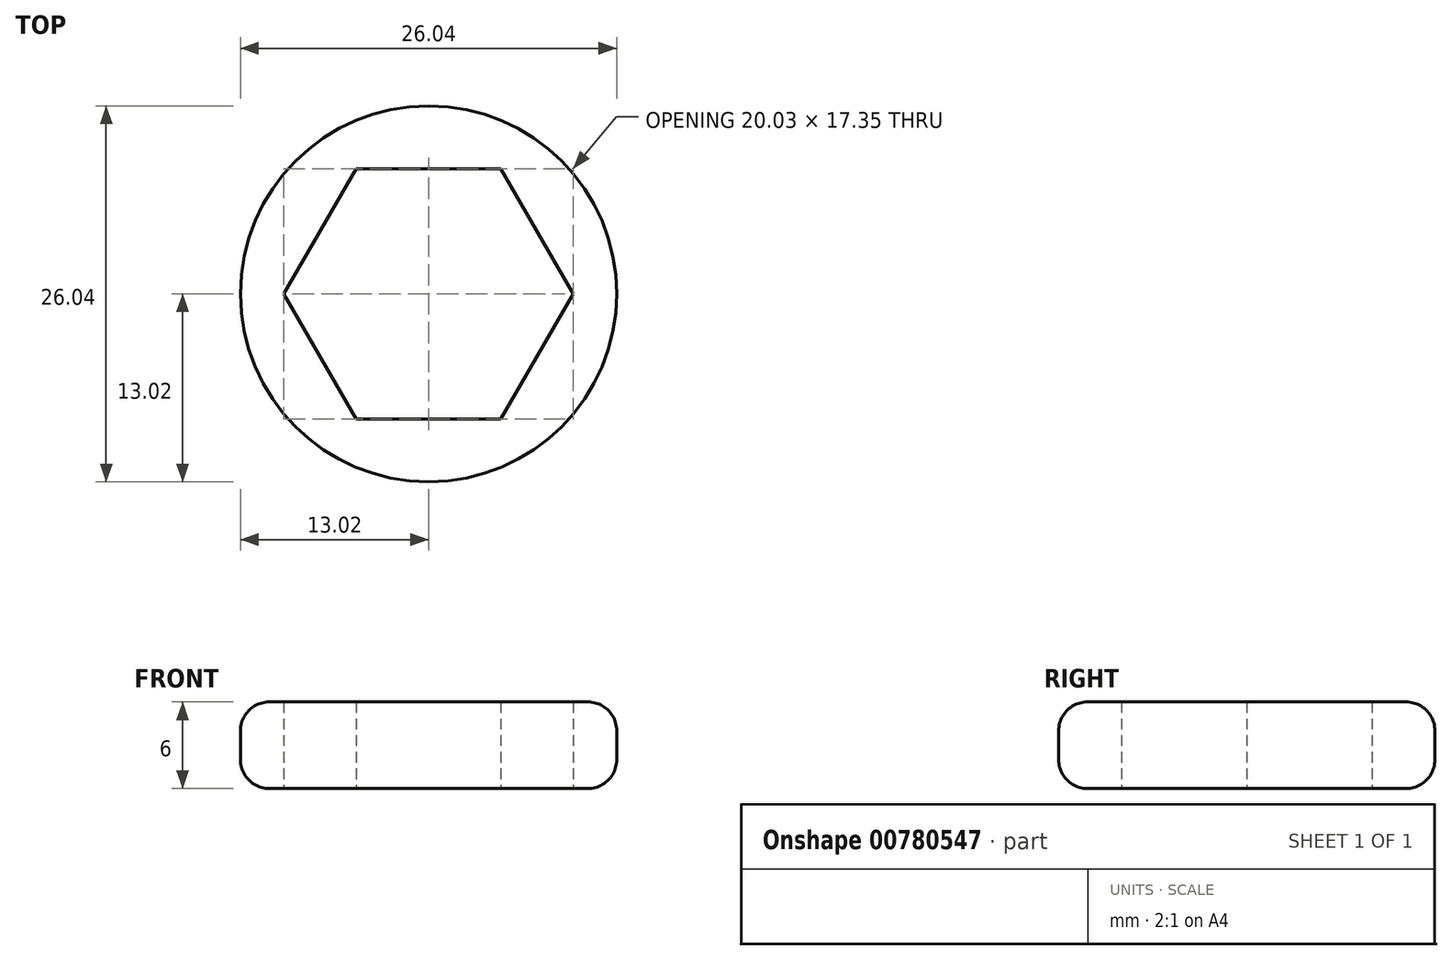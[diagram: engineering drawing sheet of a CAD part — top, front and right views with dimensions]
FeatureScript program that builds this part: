
annotation { "Feature Type Name" : "Feature", "Feature Type Description" : "" }
export const myFeature = defineFeature(function(context is Context, id is Id, definition is map)
    precondition{}
    {
        {
            var Q0;
            Q0=qCreatedBy(makeId("Top.planeOp"),FACE);
            var sketch = newSketch(context, id + "F0", { "sketchPlane" : qUnion([Q0])});
            skCircle(sketch, "E0.cCircle", {"center": v(0, 0) * mm, "radius": 8.68 * mm, "construction": true});
            skLineSegment(sketch, "E0.0", {"start": v(-5, 8.68) * mm, "end": v(5, 8.68) * mm});
            skLineSegment(sketch, "E0.1", {"start": v(5, 8.68) * mm, "end": v(10.02, 0) * mm});
            skLineSegment(sketch, "E0.2", {"start": v(10.02, 0) * mm, "end": v(5, -8.68) * mm});
            skLineSegment(sketch, "E0.3", {"start": v(5, -8.68) * mm, "end": v(-5, -8.68) * mm});
            skLineSegment(sketch, "E0.4", {"start": v(-5, -8.68) * mm, "end": v(-10.02, 0) * mm});
            skLineSegment(sketch, "E0.5", {"start": v(-10.02, 0) * mm, "end": v(-5, 8.68) * mm});
            skPoint(sketch, "E0.0.midPoint", {"position": v(0, 8.68) * mm});
            skCircle(sketch, "E1", {"center": v(0, 0) * mm, "radius": 13.02 * mm});
            skSolve(sketch);
        }
        {
            var Q0;
            Q0=qSketchRegion(id+"F0",true);
            extrude(context, id + "F1", {"entities" : qUnion([Q0]), "depth" : 6 * mm, "offsetDistance" : 25 * mm});
        }
        {
            var Q0;
            Q0=makeQuery(id+"F1.opExtrude","CAP_EDGE",EDGE,{"disambiguationData":[OSD([sQuery(id+"F0.wireOp",EDGE,"E1")])],"isStart":false});
            var Q1;
            Q1=makeQuery(id+"F1.opExtrude","CAP_EDGE",EDGE,{"disambiguationData":[OSD([sQuery(id+"F0.wireOp",EDGE,"E1")])],"isStart":true});
            fillet(context, id + "F2", {"entities" : qUnion([Q0, Q1]), "radius" : 2 * mm, "tangentPropagation" : true, "allowEdgeOverflow" : false});
        }
    });
